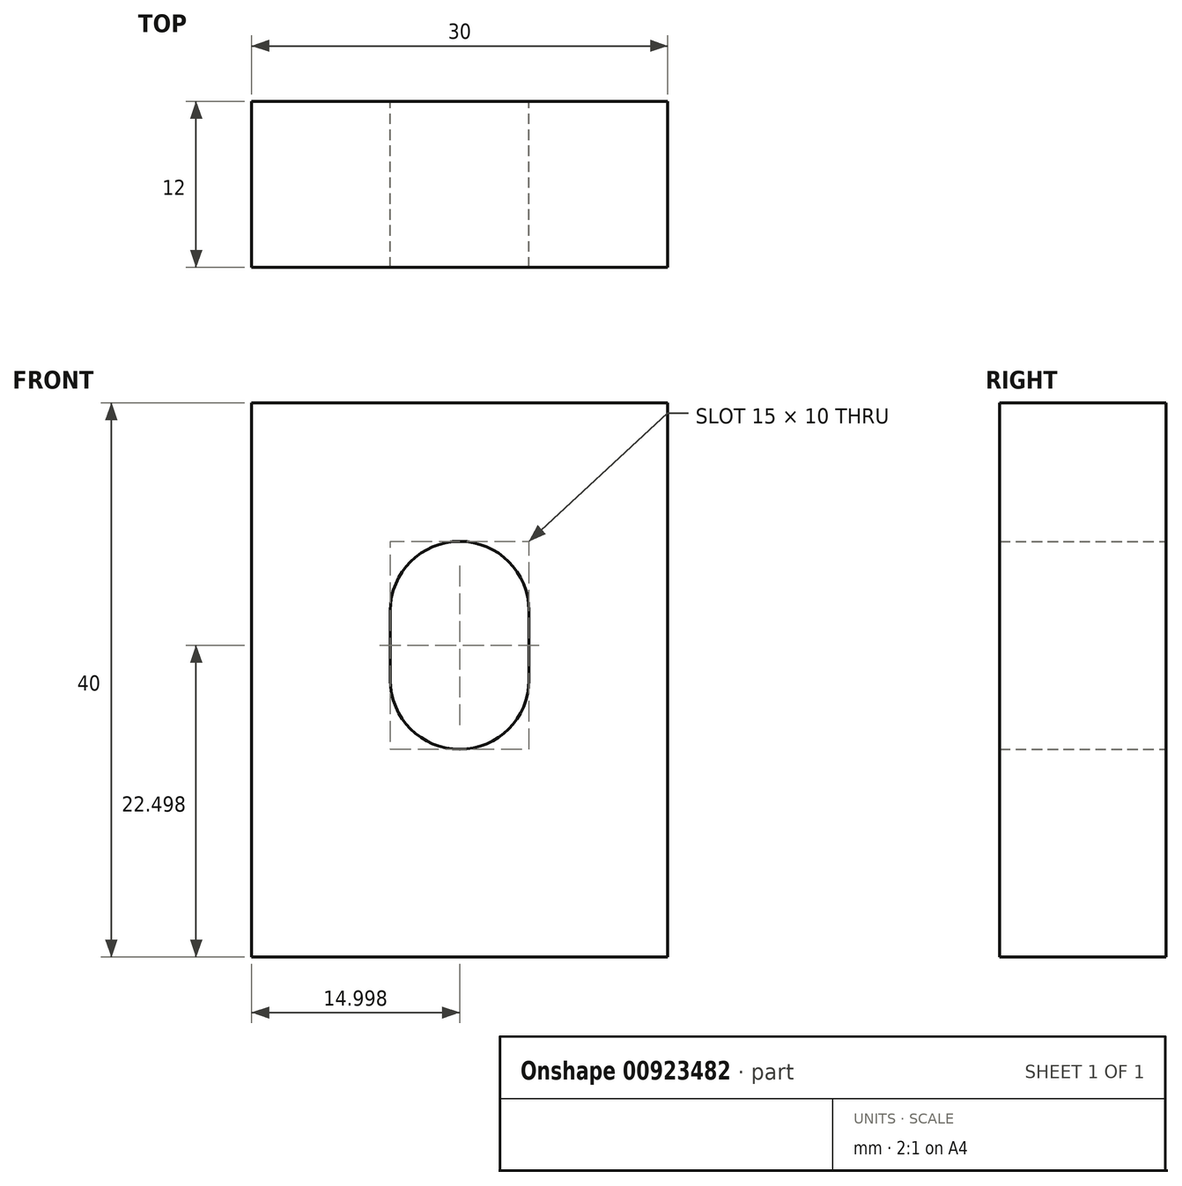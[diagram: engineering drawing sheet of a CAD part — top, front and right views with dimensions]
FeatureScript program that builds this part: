
annotation { "Feature Type Name" : "Feature", "Feature Type Description" : "" }
export const myFeature = defineFeature(function(context is Context, id is Id, definition is map)
    precondition{}
    {
        {
            var Q0;
            Q0=qCreatedBy(makeId("Front.planeOp"),FACE);
            var sketch = newSketch(context, id + "F0", { "sketchPlane" : qUnion([Q0])});
            skLineSegment(sketch, "E0.bottom", {"start": v(-47.4, 51.84) * mm, "end": v(-17.4, 51.84) * mm});
            skLineSegment(sketch, "E0.top", {"start": v(-47.4, 11.84) * mm, "end": v(-17.4, 11.84) * mm});
            skLineSegment(sketch, "E0.left", {"start": v(-47.4, 51.84) * mm, "end": v(-47.4, 11.84) * mm});
            skLineSegment(sketch, "E0.right", {"start": v(-17.4, 51.84) * mm, "end": v(-17.4, 11.84) * mm});
            skArc(sketch, "E1", {"start": v(-27.4, 36.84) * mm, "mid": v(-32.4, 41.84) * mm, "end": v(-37.4, 36.84) * mm});
            skPoint(sketch, "E1.centerSnap0", {"position": v(-32.4, 51.84) * mm});
            skArc(sketch, "E2", {"start": v(-37.4, 31.84) * mm, "mid": v(-32.4, 26.84) * mm, "end": v(-27.4, 31.84) * mm});
            skLineSegment(sketch, "E3", {"start": v(-27.4, 36.84) * mm, "end": v(-27.4, 31.84) * mm});
            skLineSegment(sketch, "E4", {"start": v(-37.4, 36.84) * mm, "end": v(-37.4, 31.84) * mm});
            skSolve(sketch);
        }
        {
            var Q0;
            Q0 = qSketchRegion(id + "F0", true);
            extrude(context, id + "F1", {"entities" : qUnion([Q0]), "depth" : 12 * mm, "offsetDistance" : 25 * mm});
        }
    });
